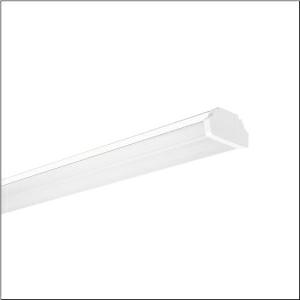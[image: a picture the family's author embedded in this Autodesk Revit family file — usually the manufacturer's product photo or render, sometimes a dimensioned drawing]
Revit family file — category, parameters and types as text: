
# Revit family: dus_r__31_gen_2_53bd812cv685c2_c333
name_source: partatom
category: Lighting Fixtures
units: mm (PartAtom-declared; Revit-internal decimal feet)

## family parameters
Cut with Voids When Loaded = No
Host = Face
Light Source = No
Part Type = Normal
Room Calculation Point = No
Round Connector Dimension = Use Diameter
Shared = No

## types (1)
- --- (1 x LED, 8970 lm, 49.9 W, 6500K)
    Apparent Load = 50 VA
    CIE Flux Codes = 47 80 95 93 100
    Color Rendering = 80
    Color Temperature = 6500K
    Default Elevation = 1800 mm
    Description = DUS® 31 Gen.2, luminaire insert, of sheet steel, coil coated, white, length: 1.535mm, width: 81mm, height: 90mm, 5x system unit, system units: 307mm, LED rated luminous flux: 8.970lm, light colour: 865, control gear: ON/OFF Multilumen, CLOi, with plug, 3-pole, with phase selection, mains connection: 220..240V, AC, 50/60Hz, start of lifetime: 50W, end of service life: 61W, through-wiring accessed according to module size, primary optical cover: cover, of PMMA, light emission: direct distribution, primary light characteristic: symmetric, protection rating (complete): IP20, protection rating (LED compartment): IP50, insulation class (complete): insulation class I (protective earthing), certification: CE, ENEC, VDE, UKCA, impact resistance: IK03, permissible ambient temperature for indoor applications: -35..+40°C, corresponds to IFS (International Featured Standards) requirements for safety and quality in the food industry, reducing of maximum allowable ambient temperature of 5°C with ceiling mounting, packaging unit: 1 piece
    Height = 95 mm
    Lamp = 1 x LED
    Lamp Light Flux = 8970 lm
    Lamp Power = 49.9 W
    Lamp count = 1
    Length = 1535 mm
    Luminous efficacy = 180 lm/W
    Manufacturer = Siteco
    ModVariant = No
    Model = 53BD812CV685C2
    Mounting Place = Ceiling
    Mounting Type = Pendant
    Number of Poles = 1
    OnlyDefault = Yes
    Power Factor = 1
    Product Name = DUS® 31 Gen.2
    Product group = luminaire insert
    ProductGroupID = 901
    Protection Class = Protection class I
    Protection Degree = IP 20
    RLX_Detail_Level = 1
    RLX_Emergency_Light_Flux = 0 lm
    RLX_Emergency_Type = 0
    RLX_Emergency_Type_DB = No
    RlxData = <blob elided: 29721 chars, md5=9d7767c1>
    Socket = socket
    Standby Power = 0 W
    System Light Flux = 8970 lm
    System Power = 50 W
    Type Comments = factory setting: luminous flux: 100 % | (A | C | E) | 116 mA
    Type Image = l_1319596.jpg
    URL = http://relux.com
    VarID = @adj_010019
    Voltage = 0 V
    Weight = 0.00 kg
    Width = 81 mm

## geometry (parser evidence)
native form markers: Blend x4, Sweep x11
no freeform markers — native parametric forms only
